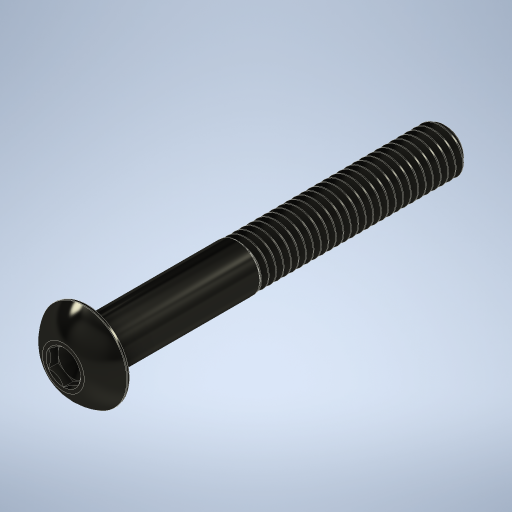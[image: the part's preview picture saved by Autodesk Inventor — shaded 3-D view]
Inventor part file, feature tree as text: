
AUTODESK INVENTOR PART (.ipt)
format: ipt  version: 2024 (Build 280153000, 153)  size: 780,800 bytes
history: native  units: in
note: dims shown in document units (in); Inventor stores cm internally (conversion verified against a paired STEP export)
features: fillet x1, other x1
ambient origin geometry x8: Origin, YZ Plane, XZ Plane, XY Plane, X Axis, Y Axis, Z Axis, Center Point
bodies: Solid1 (feature_tree), Solid2 (feature_tree)
feature tree (2):
  fillet  "Fillet2"  [1 undecoded]
  other  "Split1[1]"
note: 1 required parameter value undecoded (feature->parameter linkage not recoverable at this tier; creation-order binding heuristic only, values carry confidence <= 0.55)
